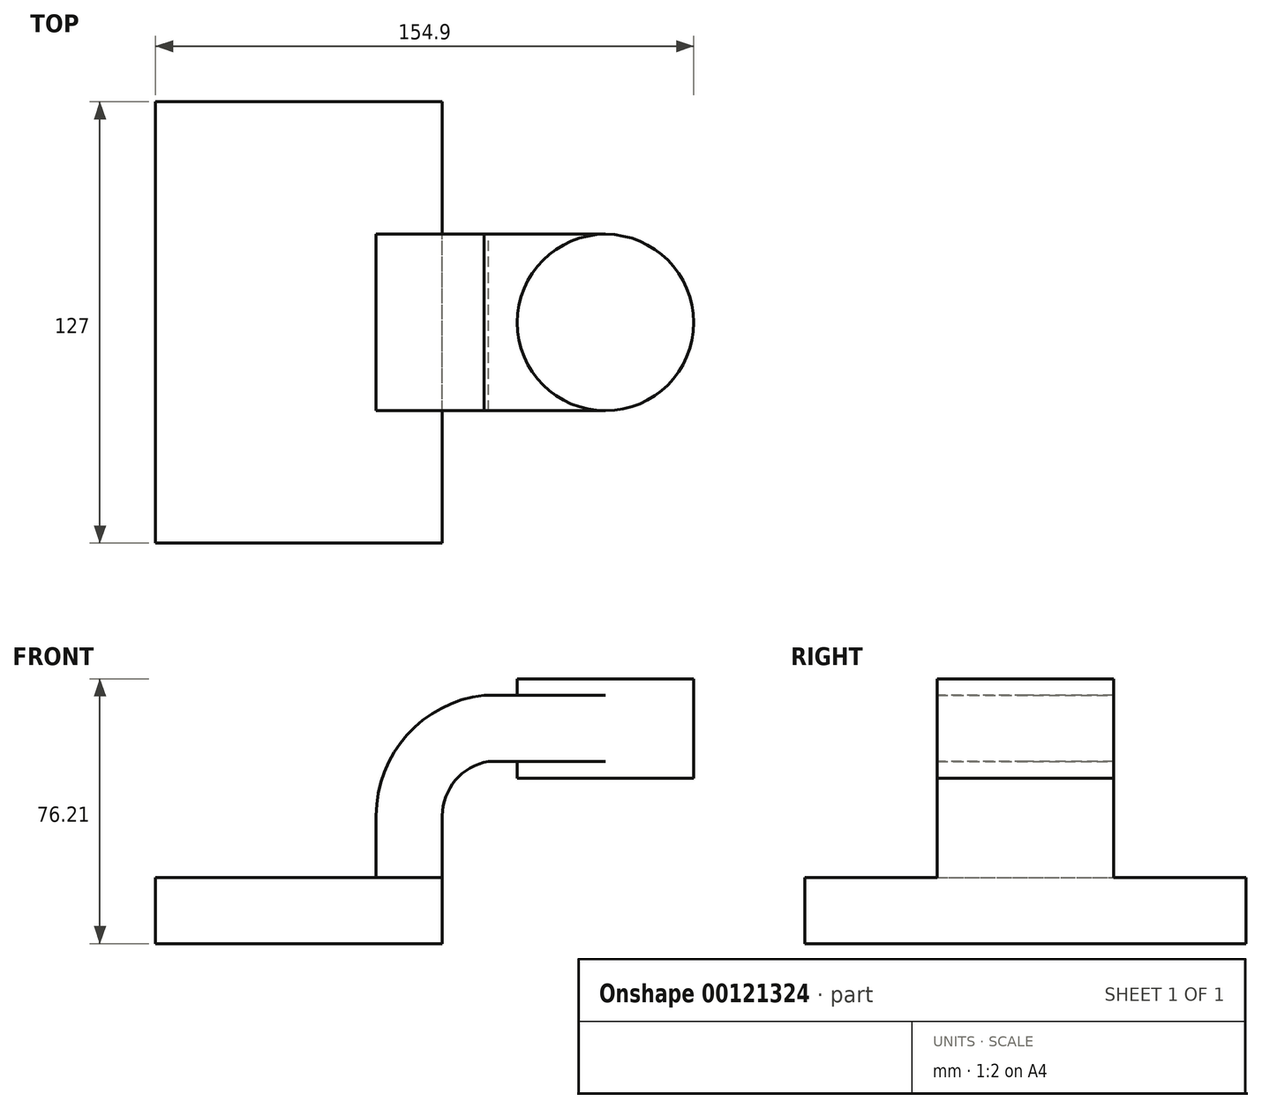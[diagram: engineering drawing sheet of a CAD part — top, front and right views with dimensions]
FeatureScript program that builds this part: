
annotation { "Feature Type Name" : "Feature", "Feature Type Description" : "" }
export const myFeature = defineFeature(function(context is Context, id is Id, definition is map)
    precondition{}
    {
        {
            var Q0;
            Q0=qCreatedBy(makeId("Front.planeOp"),FACE);
            var sketch = newSketch(context, id + "F0", { "sketchPlane" : qUnion([Q0])});
            skLineSegment(sketch, "E0.bottom", {"start": v(-41.28, -9.52) * mm, "end": v(41.28, -9.52) * mm});
            skLineSegment(sketch, "E0.top", {"start": v(-41.28, 9.52) * mm, "end": v(41.27, 9.52) * mm});
            skLineSegment(sketch, "E0.left", {"start": v(-41.27, -9.52) * mm, "end": v(-41.28, 9.52) * mm});
            skLineSegment(sketch, "E0.right", {"start": v(41.28, -9.52) * mm, "end": v(41.27, 9.52) * mm});
            skPoint(sketch, "E0.middle", {"position": v(0, 0) * mm});
            skLineSegment(sketch, "E1.bottom", {"start": v(113.62, 38.1) * mm, "end": v(62.82, 38.1) * mm});
            skLineSegment(sketch, "E1.top", {"start": v(113.62, 66.68) * mm, "end": v(62.82, 66.68) * mm});
            skLineSegment(sketch, "E1.left", {"start": v(113.62, 38.1) * mm, "end": v(113.62, 66.68) * mm});
            skLineSegment(sketch, "E1.right", {"start": v(62.82, 38.1) * mm, "end": v(62.82, 66.68) * mm});
            skPoint(sketch, "E1.middle", {"position": v(88.22, 52.39) * mm});
            skLineSegment(sketch, "E2", {"start": v(41.27, 9.52) * mm, "end": v(41.27, 27.22) * mm});
            skArc(sketch, "E3", {"start": v(41.27, 27.22) * mm, "mid": v(45.04, 37.48) * mm, "end": v(54.54, 42.88) * mm});
            skLineSegment(sketch, "E4", {"start": v(54.54, 42.88) * mm, "end": v(88.22, 42.88) * mm});
            skLineSegment(sketch, "E5.0", {"start": v(53.28, 61.93) * mm, "end": v(88.22, 61.93) * mm});
            skArc(sketch, "E5.1", {"start": v(22.22, 27.22) * mm, "mid": v(31.12, 50.5) * mm, "end": v(53.28, 61.93) * mm});
            skLineSegment(sketch, "E5.2", {"start": v(22.22, 9.52) * mm, "end": v(22.22, 27.22) * mm});
            skLineSegment(sketch, "E6", {"start": v(88.22, 61.93) * mm, "end": v(88.22, 42.88) * mm});
            skFitSpline(sketch, "E7", {"points": [v(-41.28, 9.53) * mm, v(53.28, 61.93) * mm], "startDerivative": vector(1.32, 126.93) * mm, "endDerivative": vector(175.34, -2.06) * mm});
            skPoint(sketch, "E8", {"position": v(88.22, 38.1) * mm});
            skLineSegment(sketch, "E9", {"start": v(88.22, 38.1) * mm, "end": v(88.22, 66.68) * mm});
            skSolve(sketch);
        }
        {
            var Q0;
            Q0=makeQuery(id+"F0.imprint","IMPRINT",FACE,{"disambiguationData":[TD([[makeQuery(id+"F0.imprint","IMPRINT",EDGE,{"derivedFrom":sQuery(id+"F0.wireOp",EDGE,"E0.bottom")}),1.0]])]});
            extrude(context, id + "F1", {"entities" : qUnion([Q0]), "endBound" : BoundingType.SYMMETRIC, "depth" : 127 * mm});
        }
        {
            var Q0;
            {var subQ0=sQuery(id+"F0.wireOp",EDGE,"E4");var subQ1=sQuery(id+"F0.wireOp",EDGE,"E1.right");var subQ2=makeQuery(id+"F0.imprint","INTERSECT",VERTEX,{"derivedFrom":[subQ1,subQ0]});Q0=makeQuery(id+"F0.imprint","IMPRINT",FACE,{"disambiguationData":[TD([[makeQuery(id+"F0.imprint","IMPRINT",EDGE,{"disambiguationData":[TD([[subQ2,-1.0]])],"derivedFrom":subQ1}),-1.0]])]});}
            var Q1;
            {var subQ1=sQuery(id+"F0.wireOp",EDGE,"E2");Q1=makeQuery(id+"F0.imprint","IMPRINT",FACE,{"disambiguationData":[TD([[makeQuery(id+"F0.imprint","IMPRINT",EDGE,{"derivedFrom":subQ1}),1.0]])]});}
            extrude(context, id + "F2", {"entities" : qUnion([Q0, Q1]), "operationType" : NewBodyOperationType.ADD, "endBound" : BoundingType.SYMMETRIC, "depth" : 50.8 * mm});
        }
        {
            var Q0;
            Q0=makeQuery(id+"F0.imprint","IMPRINT",FACE,{"disambiguationData":[TD([[makeQuery(id+"F0.imprint","IMPRINT",EDGE,{"derivedFrom":sQuery(id+"F0.wireOp",EDGE,"E5.1")}),1.0]])]});
            extrude(context, id + "F3", {"entities" : qUnion([Q0]), "operationType" : NewBodyOperationType.ADD, "endBound" : BoundingType.SYMMETRIC, "depth" : 15.88 * mm});
        }
        {
            var Q0;
            {var subQ0=sQuery(id+"F0.wireOp",EDGE,"E1.left");Q0=makeQuery(id+"F0.imprint","IMPRINT",FACE,{"disambiguationData":[TD([[makeQuery(id+"F0.imprint","IMPRINT",EDGE,{"derivedFrom":subQ0}),1.0]])]});}
            var Q1;
            Q1=sQuery(id+"F0.wireOp",EDGE,"E9");
            revolve(context, id + "F4", {"operationType" : NewBodyOperationType.ADD, "entities" : qUnion([Q0]), "axis" : qUnion([Q1]), "revolveType" : RevolveType.FULL});
        }
    });
